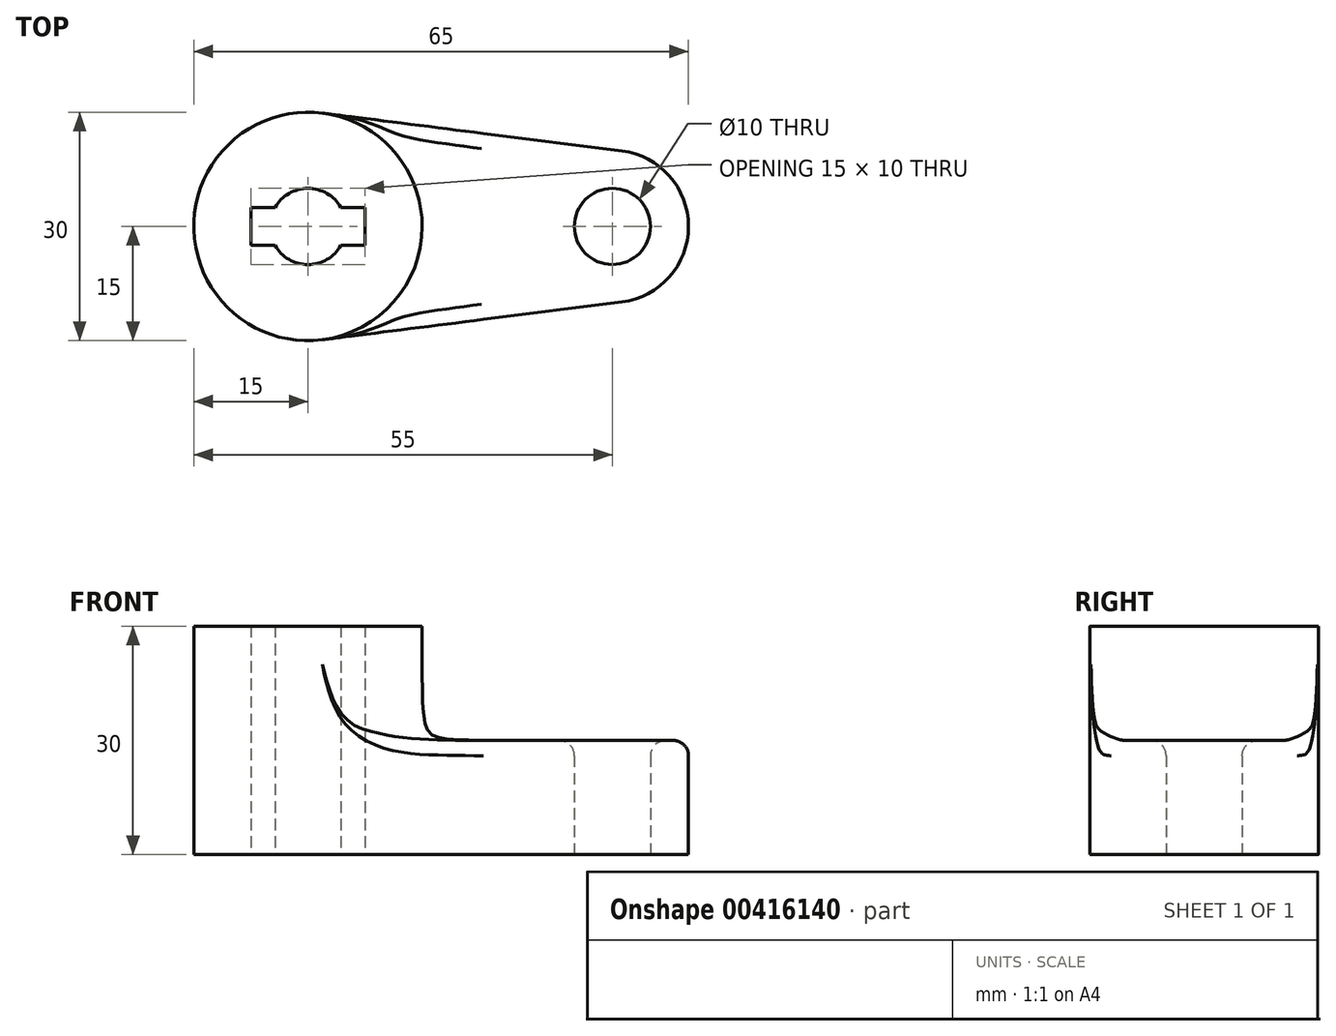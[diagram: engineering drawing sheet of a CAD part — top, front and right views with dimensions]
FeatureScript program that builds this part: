
annotation { "Feature Type Name" : "Feature", "Feature Type Description" : "" }
export const myFeature = defineFeature(function(context is Context, id is Id, definition is map)
    precondition{}
    {
        {
            var Q0;
            Q0=qCreatedBy(makeId("Top.planeOp"),FACE);
            var sketch = newSketch(context, id + "F0", { "sketchPlane" : qUnion([Q0])});
            skCircle(sketch, "E0", {"center": v(-20, 0) * mm, "radius": 15 * mm});
            skCircle(sketch, "E1", {"center": v(20, 0) * mm, "radius": 10 * mm});
            skCircle(sketch, "E2", {"center": v(20, 0) * mm, "radius": 5 * mm});
            skCircle(sketch, "E3", {"center": v(-20, 0) * mm, "radius": 5 * mm});
            skLineSegment(sketch, "E4", {"start": v(-18.13, 14.88) * mm, "end": v(21.25, 9.92) * mm});
            skLineSegment(sketch, "E5", {"start": v(21.25, -9.92) * mm, "end": v(-18.13, -14.88) * mm});
            skLineSegment(sketch, "E6", {"start": v(-20, 0) * mm, "end": v(20, 0) * mm, "construction": true});
            skLineSegment(sketch, "E7.bottom", {"start": v(-12.5, -2.5) * mm, "end": v(-27.5, -2.5) * mm});
            skLineSegment(sketch, "E7.top", {"start": v(-12.5, 2.5) * mm, "end": v(-27.5, 2.5) * mm});
            skLineSegment(sketch, "E7.left", {"start": v(-12.5, -2.5) * mm, "end": v(-12.5, 2.5) * mm});
            skLineSegment(sketch, "E7.right", {"start": v(-27.5, -2.5) * mm, "end": v(-27.5, 2.5) * mm});
            skSolve(sketch);
        }
        {
            var Q0;
            {var subQ11=sQuery(id+"F0.wireOp",EDGE,"E7.left");Q0=makeQuery(id+"F0.imprint","IMPRINT",FACE,{"disambiguationData":[TD([[makeQuery(id+"F0.imprint","IMPRINT",EDGE,{"derivedFrom":subQ11}),-1.0]])]});}
            var Q1;
            {var subQ0=sQuery(id+"F0.wireOp",EDGE,"E4");Q1=makeQuery(id+"F0.imprint","IMPRINT",FACE,{"disambiguationData":[TD([[makeQuery(id+"F0.imprint","IMPRINT",EDGE,{"derivedFrom":subQ0}),-1.0]])]});}
            var Q2;
            Q2=makeQuery(id+"F0.imprint","IMPRINT",FACE,{"disambiguationData":[TD([[makeQuery(id+"F0.imprint","IMPRINT",EDGE,{"derivedFrom":sQuery(id+"F0.wireOp",EDGE,"E2")}),-1.0]])]});
            extrude(context, id + "F1", {"entities" : qUnion([Q0, Q1, Q2]), "depth" : 15 * mm, "offsetDistance" : 25 * mm});
        }
        {
            var Q0;
            {var subQ11=sQuery(id+"F0.wireOp",EDGE,"E7.left");Q0=makeQuery(id+"F0.imprint","IMPRINT",FACE,{"disambiguationData":[TD([[makeQuery(id+"F0.imprint","IMPRINT",EDGE,{"derivedFrom":subQ11}),-1.0]])]});}
            extrude(context, id + "F2", {"entities" : qUnion([Q0]), "operationType" : NewBodyOperationType.ADD, "depth" : 30 * mm, "offsetDistance" : 25 * mm});
        }
        {
            var Q0;
            {var subQ0=sQuery(id+"F0.wireOp",EDGE,"E0");Q0=makeQuery(id+"F2.boolean.opBoolean","INTERSECT",EDGE,{"derivedFrom":[makeQuery(id+"F1.opExtrude","CAP_FACE",FACE,{"disambiguationData":[OSD([subQ0,sQuery(id+"F0.wireOp",EDGE,"E1"),sQuery(id+"F0.wireOp",EDGE,"E2"),sQuery(id+"F0.wireOp",EDGE,"E3"),sQuery(id+"F0.wireOp",EDGE,"E4"),sQuery(id+"F0.wireOp",EDGE,"E5"),sQuery(id+"F0.wireOp",EDGE,"E7.bottom"),sQuery(id+"F0.wireOp",EDGE,"E7.top"),sQuery(id+"F0.wireOp",EDGE,"E7.left"),sQuery(id+"F0.wireOp",EDGE,"E7.right")])],"isStart":false}),makeQuery(id+"F2.opExtrude","SWEPT_FACE",FACE,{"disambiguationData":[OSD([subQ0])]})]});}
            fillet(context, id + "F3", {"entities" : qUnion([Q0]), "radius" : 10 * mm, "rho" : .8, "crossSection" : FilletCrossSection.CONIC, "allowEdgeOverflow" : false});
        }
        {
            var Q0;
            Q0=makeQuery(id+"F1.opExtrude","CAP_FACE",FACE,{"disambiguationData":[OSD([sQuery(id+"F0.wireOp",EDGE,"E0"),sQuery(id+"F0.wireOp",EDGE,"E1"),sQuery(id+"F0.wireOp",EDGE,"E2"),sQuery(id+"F0.wireOp",EDGE,"E3"),sQuery(id+"F0.wireOp",EDGE,"E4"),sQuery(id+"F0.wireOp",EDGE,"E5"),sQuery(id+"F0.wireOp",EDGE,"E7.bottom"),sQuery(id+"F0.wireOp",EDGE,"E7.top"),sQuery(id+"F0.wireOp",EDGE,"E7.left"),sQuery(id+"F0.wireOp",EDGE,"E7.right")])],"isStart":false});
            fillet(context, id + "F4", {"entities" : qUnion([Q0]), "radius" : 2 * mm, "tangentPropagation" : true, "allowEdgeOverflow" : false});
        }
    });
